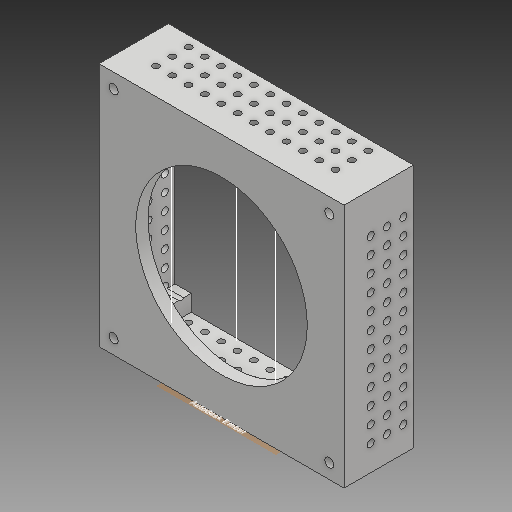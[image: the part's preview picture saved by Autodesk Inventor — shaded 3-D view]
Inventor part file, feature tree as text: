
AUTODESK INVENTOR PART (.ipt)
format: ipt  version: 2018 (Build 220112000, 112)  size: 536,064 bytes
history: native  units: mm
features: sketch x13, extrude x8, pattern_linear x3
ambient origin geometry x8: Origin, YZ Plane, XZ Plane, XY Plane, X Axis, Y Axis, Z Axis, Center Point
bodies: Solid1 (feature_tree)
feature tree (24):
  sketch  "Sketch1"  dims[d0=150.0mm d1=150.0mm]
  extrude  "Extrusion1"  Depth=150.0mm
  extrude  "Extrusion3"  Depth=4.0mm
  extrude  "Extrusion4"  Depth=10.0mm
  pattern_linear  "Rectangular Pattern1"  Count1=2 Spacing1=132.0mm
  extrude  "Extrusion5"  Depth=80.0mm
  pattern_linear  "Rectangular Pattern2"  Count1=8 Spacing1=0.0mm
  sketch  "Sketch9"  dims[d17=20.0mm d19=132.0mm d20=5.5mm d21=80.0mm d22=0.0mm]
  extrude  "Extrusion8"  Depth=132.0mm
  sketch  "Sketch11"  dims[d45=70.0mm d46=0.0mm d47=6.5mm d48=70.0mm d49=0.0mm]
  extrude  "Extrusion9"  Depth=6.5mm
  pattern_linear  "Rectangular Pattern5"  Count1=7 Spacing1=0.0mm
  extrude  "Extrusion10"  Depth=80.0mm
  sketch  "Sketch14"  dims[d57=12.5mm]
  sketch  "Sketch15"  dims[d58=70.0mm d59=0.0mm]
  extrude  "Extrusion11"  Depth=7.5mm TaperAngle=0.0deg
  sketch  "Sketch2"  dims[d2=7.5mm d3=0.0mm d7=4.0mm]
  sketch  "Sketch4"  dims[d8=35.0mm d9=0.0mm d10=10.0mm]
  sketch  "Sketch5"  dims[d11=10.0mm]
  sketch  "Sketch6"  dims[d12=35.0mm d13=0.0mm d14=20.0mm d16=132.0mm]
  sketch  "Sketch10"  dims[d23=20.0mm d25=132.0mm d26=20.0mm d28=132.0mm]
  sketch  "Sketch12"  dims[d50=30.0mm d52=10.0mm d53=80.0mm]
  sketch  "Sketch13"  dims[d54=7.5mm d55=70.0mm d56=0.0mm]
  sketch  "Sketch16"
